# Revit family: Caribou_Elara 3_0
name_source: partatom
category: Lighting Fixtures
units: mm (PartAtom-declared; Revit-internal decimal feet)

## family parameters
Always vertical = Yes
Cut with Voids When Loaded = No
Light Source = Yes
Maintain Annotation Orientation = No
OmniClass Number = 23.80.70.00
OmniClass Title = Lighting
Part Type = Normal
Room Calculation Point = No
Round Connector Dimension = Use Diameter
Shared = No
Work Plane-Based = No

## types (2) — shared parameters
Color Filter = 16777215
Dimming Lamp Color Temperature Shift = <None>
Light Source Symbol Size = 610 mm
Light_Material = Light
Manufacturer = Caribou
Model = Elara 3.0
zero-valued in all types: Default Elevation

## per-type parameters (varying)
| type | Finishes |
| Flat White | Caribou_Flat White |
| Ace Black | Caribou_Ace Black |

note: column(s) folded — value = type name in every type: Description

## geometry (parser evidence)
native form markers: Sweep x3
no freeform markers — native parametric forms only
